# Revit family: SURVIVOR130xxWS840SAS0500x
name_source: partatom
category: Leuchten
units: mm (PartAtom-declared; Revit-internal decimal feet)

## family parameters
Basisbauteil = Fläche
Beim Laden mit Abzugskörper schneiden = Nein
Bemaßung runder Anschluss = Durchmesser verwenden
Gemeinsam genutzt = Nein
Lichtquelle = Ja
OmniClass-Nummer = 23.80.70.11
OmniClass-Titel = Luminaries for Internal Lighting
Raumberechnungspunkt = Nein
Teiletyp = Normal

## types (2) — shared parameters
Baugruppenkennzeichen = D5020200
Datei für fotometrisches Netz = SURVIVOR_SAS.IES
Emissionsform beim Rendern sichtbar = Nein
Farbfilter = 16777215
Farbtemperaturverschiebung bei Dämpfen der Lampe = <Keine Auswahl>
Hersteller = RIDI Leuchten GmbH
Lampe = LED
Neigungswinkel = 90.00°
URL = www.ridi.de
Von Breite des Rechtecks ausssenden = 1228 mm  [stored 4.02887 ft]
Von Länge des Rechtecks aussenden = 181 mm  [stored 0.593832 ft]
brand = RIDI
conformity mark = CE
electrical safety class = 1
height = 73 mm  [stored 0.239501 ft]
ingress protection (IP) code = IP65
length = 1300 mm  [stored 4.26509 ft]
nominal frequency = 50-60Hz
nominal voltage = 230
voltage type (AC, DC, UC) = AC
weight = 11
width = 240 mm  [stored 0.787402 ft]
zero-valued in all types: Vorgabe-Ansicht

## per-type parameters (varying)
| type | Modell | Scheinlast | rated input power |
| SURVIVOR130DAWS840SAS0500 | 0632216 | 35 VA | 35 |
| SURVIVOR130NDWS840SAS0500-RF | 0622216//420 | 34 VA | 34 |

note: column(s) folded — value = type name in every type: product name

note: [stored X ft] marks values corroborated as IEEE doubles in the binary element streams (Revit-internal decimal feet)
